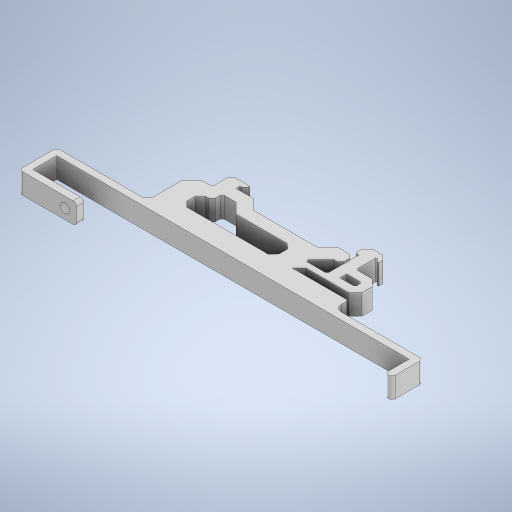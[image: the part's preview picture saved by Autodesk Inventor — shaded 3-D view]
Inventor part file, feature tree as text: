
AUTODESK INVENTOR PART (.ipt)
format: ipt  version: 2024 (Build 280153000, 153)  size: 460,800 bytes
history: native  units: in
note: dims shown in document units (in); Inventor stores cm internally (conversion verified against a paired STEP export)
features: extrude x3, sketch x3, fillet x2, projected_geometry x1
ambient origin geometry x8: Origin, YZ Plane, XZ Plane, XY Plane, X Axis, Y Axis, Z Axis, Center Point
bodies: Solid1 (feature_tree)
feature tree (9):
  extrude  "Extrusion1"  Depth=0.0394in
  fillet  "Fillet3"  Radius=4.2126in
  extrude  "Extrusion3"  Depth=1.0455in
  fillet  "Fillet4"  Radius=0.2362in
  extrude  "Extrusion4"  Depth=0.0787in
  sketch  "Sketch1"  dims[d8=0.2362in d9=0.0in]
  sketch  "Sketch3"  dims[d18=0.3758in d19=0.1566in d20=0.1762in d21=0.1957in d22=0.1387in d23=0.1174in d24=0.0391in d25=0.0157in d26=2.1217in d27=0.0973in d28=0.0587in d29=0.0587in d30=0.0548in d31=0.0235in d32=0.9395in d33=0.0587in d34=0.0973in d35=0.5854in d36=0.1174in d37=0.7438in d38=0.1174in d39=0.1174in d40=0.137in d41=0.1475in d42=0.0277in d43=0.2143in d44=0.3464in d45=0.0196in d46=0.0626in d47=0.0137in d48=0.0274in d49=0.0607in d50=0.1213in d51=0.047in d52=0.0509in d53=0.0157in d54=0.0356in d55=0.0094in d56=0.2063in d57=0.0196in d58=0.1664in d59=0.0783in d60=0.1174in d61=0.0783in d62=0.4893in d63=0.0783in d64=0.6302in d65=0.0156in d66=0.1253in d67=0.1174in d68=0.1174in d69=0.1174in d70=0.0391in d71=0.0391in d72=0.0391in d73=0.1475in d74=0.0695in d75=0.0391in d76=0.0391in d77=0.0196in d78=0.0196in d79=0.0196in d80=0.0196in d81=0.0196in d82=0.0658in d83=0.0235in d84=0.0587in d85=0.0391in d86=0.0391in d87=0.0391in d88=0.0626in d89=0.0548in d90=0.0156in d91=0.0471in d92=0.0607in d93=0.0137in d94=0.0196in d95=0.094in d96=0.0196in d97=0.0156in d98=0.1376in d99=0.0352in d100=0.2349in d101=0.1566in d102=0.3568in d103=0.1566in d104=0.0115in d105=0.0156in d106=0.0772in d107=0.1751in d108=0.0984in d109=0.118in]
  sketch  "Sketch4"  dims[d110=4.0551in d111=0.2756in d112=0.0787in d113=0.0787in d114=0.0787in d115=0.0787in d116=0.6614in d117=0.2756in d122=0.0394in d123=4.2126in d124=1.0455in d125=0.2362in d126=0.0in d127=0.0787in d128=0.1043in d129=0.2362in d130=0.4518in d131=0.1181in d133=0.3937in d134=0.0in]
  projected_geometry  "Projected Loop5"
